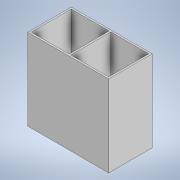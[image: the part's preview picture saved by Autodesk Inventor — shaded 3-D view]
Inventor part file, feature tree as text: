
AUTODESK INVENTOR PART (.ipt)
format: ipt  version: 2020 (Build 240168000, 168)  size: 260,096 bytes
history: native  units: mm
features: extrude x3, sketch x2
ambient origin geometry x8: Origin, YZ Plane, XZ Plane, XY Plane, X Axis, Y Axis, Z Axis, Center Point
bodies: Solid1 (feature_tree)
feature tree (5):
  extrude  "Extrusion1"  Depth=40.0mm
  sketch  "Sketch3"  dims[d2=75.0mm d3=0.0mm d10=1.5mm d11=1.5mm d12=1.5mm d13=1.5mm d14=1.5mm d15=35.0mm d16=35.0mm d17=73.5mm d18=0.0mm d19=73.5mm d20=0.0mm d21=0.5mm d22=0.872665mm]
  extrude  "Extrusion3"  Depth=1.5mm
  extrude  "Extrusion4"  Depth=1.5mm
  sketch  "Sketch1"  dims[d0=74.5mm d1=40.0mm]
